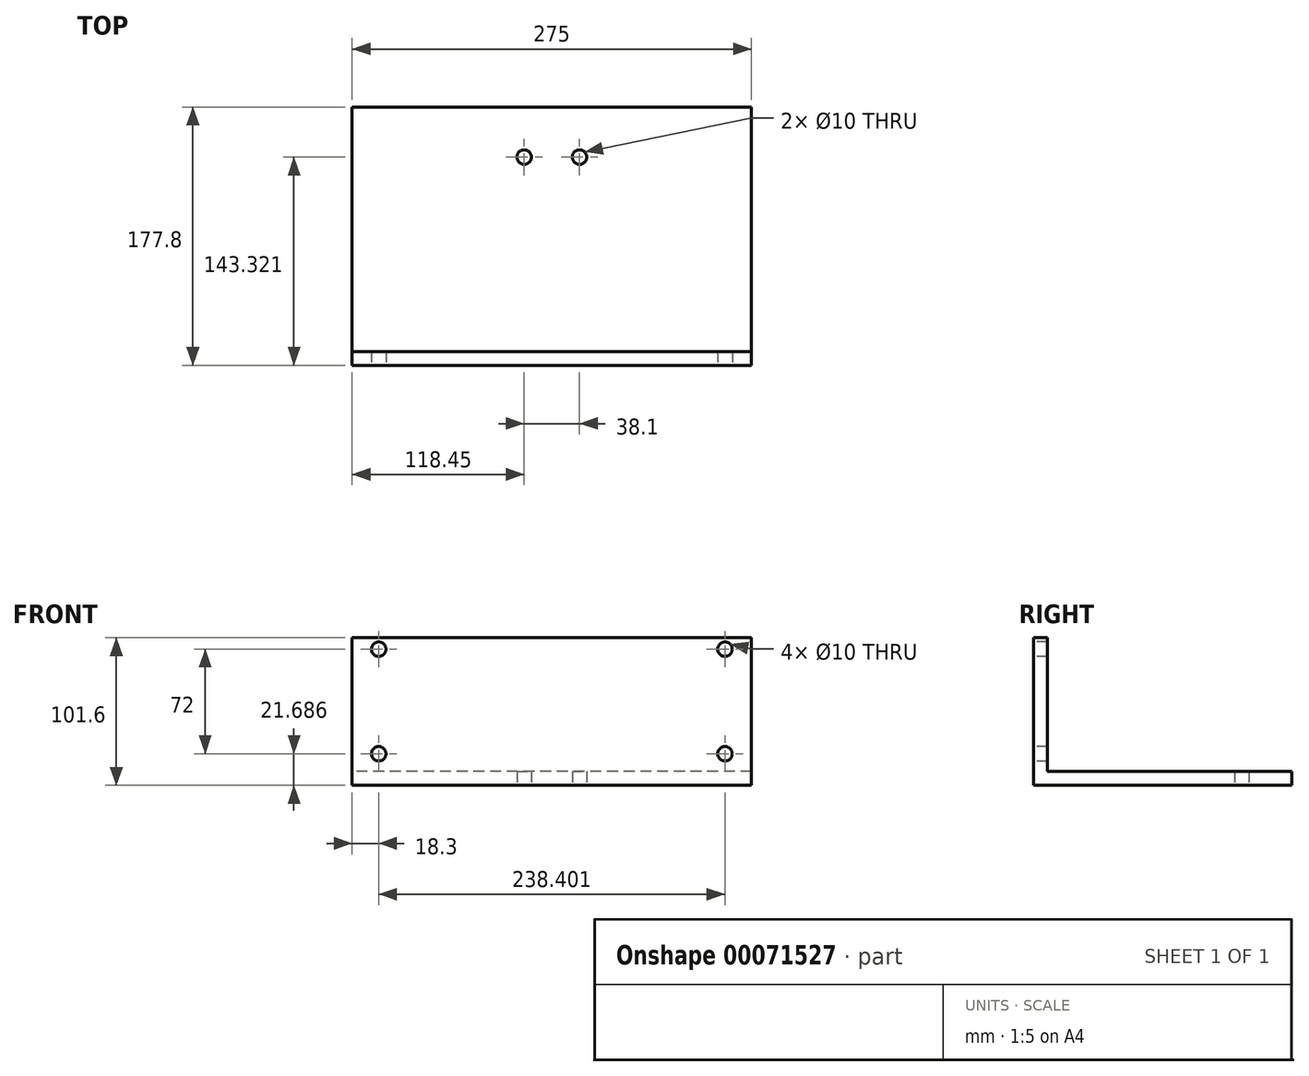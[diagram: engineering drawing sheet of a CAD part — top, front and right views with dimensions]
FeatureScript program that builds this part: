
annotation { "Feature Type Name" : "Feature", "Feature Type Description" : "" }
export const myFeature = defineFeature(function(context is Context, id is Id, definition is map)
    precondition{}
    {
        {
            var Q0;
            Q0=qCreatedBy(makeId("Front.planeOp"),FACE);
            var sketch = newSketch(context, id + "F0", { "sketchPlane" : qUnion([Q0])});
            skLineSegment(sketch, "E0.bottom", {"start": v(-148.45, -52.16) * mm, "end": v(126.55, -52.16) * mm});
            skLineSegment(sketch, "E0.top", {"start": v(-148.45, -153.76) * mm, "end": v(126.55, -153.76) * mm});
            skLineSegment(sketch, "E0.left", {"start": v(-148.45, -52.16) * mm, "end": v(-148.45, -153.76) * mm});
            skLineSegment(sketch, "E0.right", {"start": v(126.55, -52.16) * mm, "end": v(126.55, -153.76) * mm});
            skSolve(sketch);
        }
        {
            var Q0;
            Q0=qSketchRegion(id+"F0",true);
            extrude(context, id + "F1", {"entities" : qUnion([Q0]), "depth" : 177.8 * mm});
        }
        {
            var Q0;
            Q0=makeQuery(id+"F1.opExtrude","CAP_FACE",FACE,{"disambiguationData":[OSD([sQuery(id+"F0.wireOp",EDGE,"E0.bottom"),sQuery(id+"F0.wireOp",EDGE,"E0.top"),sQuery(id+"F0.wireOp",EDGE,"E0.left"),sQuery(id+"F0.wireOp",EDGE,"E0.right")])],"isStart":false});
            var sketch = newSketch(context, id + "F2", { "sketchPlane" : qUnion([Q0])});
            skCircle(sketch, "E1", {"center": v(-130.15, -60.07) * mm, "radius": 5 * mm});
            skCircle(sketch, "E2", {"center": v(-130.15, -132.07) * mm, "radius": 5 * mm});
            skCircle(sketch, "E3", {"center": v(108.25, -132.07) * mm, "radius": 5 * mm});
            skCircle(sketch, "E4", {"center": v(108.25, -60.07) * mm, "radius": 5 * mm});
            skSolve(sketch);
        }
        {
            var Q0;
            Q0=qSketchRegion(id+"F2",true);
            extrude(context, id + "F3", {"entities" : qUnion([Q0]), "operationType" : NewBodyOperationType.REMOVE, "oppositeDirection" : true, "depth" : 25 * mm});
        }
        {
            var Q0;
            Q0=makeQuery(id+"F1.opExtrude","SWEPT_FACE",FACE,{"disambiguationData":[OSD([sQuery(id+"F0.wireOp",EDGE,"E0.left")])]});
            var sketch = newSketch(context, id + "F4", { "sketchPlane" : qUnion([Q0])});
            skLineSegment(sketch, "E5.bottom", {"start": v(0, -52.16) * mm, "end": v(168.27, -52.16) * mm});
            skLineSegment(sketch, "E5.top", {"start": v(0, -144.24) * mm, "end": v(168.28, -144.24) * mm});
            skLineSegment(sketch, "E5.left", {"start": v(0, -52.16) * mm, "end": v(0, -144.24) * mm});
            skLineSegment(sketch, "E5.right", {"start": v(168.27, -52.16) * mm, "end": v(168.28, -144.24) * mm});
            skSolve(sketch);
        }
        {
            var Q0;
            Q0=qSketchRegion(id+"F4",true);
            extrude(context, id + "F5", {"entities" : qUnion([Q0]), "operationType" : NewBodyOperationType.REMOVE, "endBound" : BoundingType.THROUGH_ALL, "oppositeDirection" : true, "depth" : 25.4 * mm});
        }
        {
            var Q0;
            Q0=makeQuery(id+"F1.opExtrude","SWEPT_FACE",FACE,{"disambiguationData":[OSD([sQuery(id+"F0.wireOp",EDGE,"E0.top")])]});
            var sketch = newSketch(context, id + "F6", { "sketchPlane" : qUnion([Q0])});
            skCircle(sketch, "E6", {"center": v(8.1, 34.48) * mm, "radius": 5 * mm});
            skCircle(sketch, "E7", {"center": v(-30, 34.48) * mm, "radius": 5 * mm});
            skSolve(sketch);
        }
        {
            var Q0;
            Q0=qSketchRegion(id+"F6",true);
            extrude(context, id + "F7", {"entities" : qUnion([Q0]), "operationType" : NewBodyOperationType.REMOVE, "oppositeDirection" : true, "depth" : 25.4 * mm});
        }
    });
